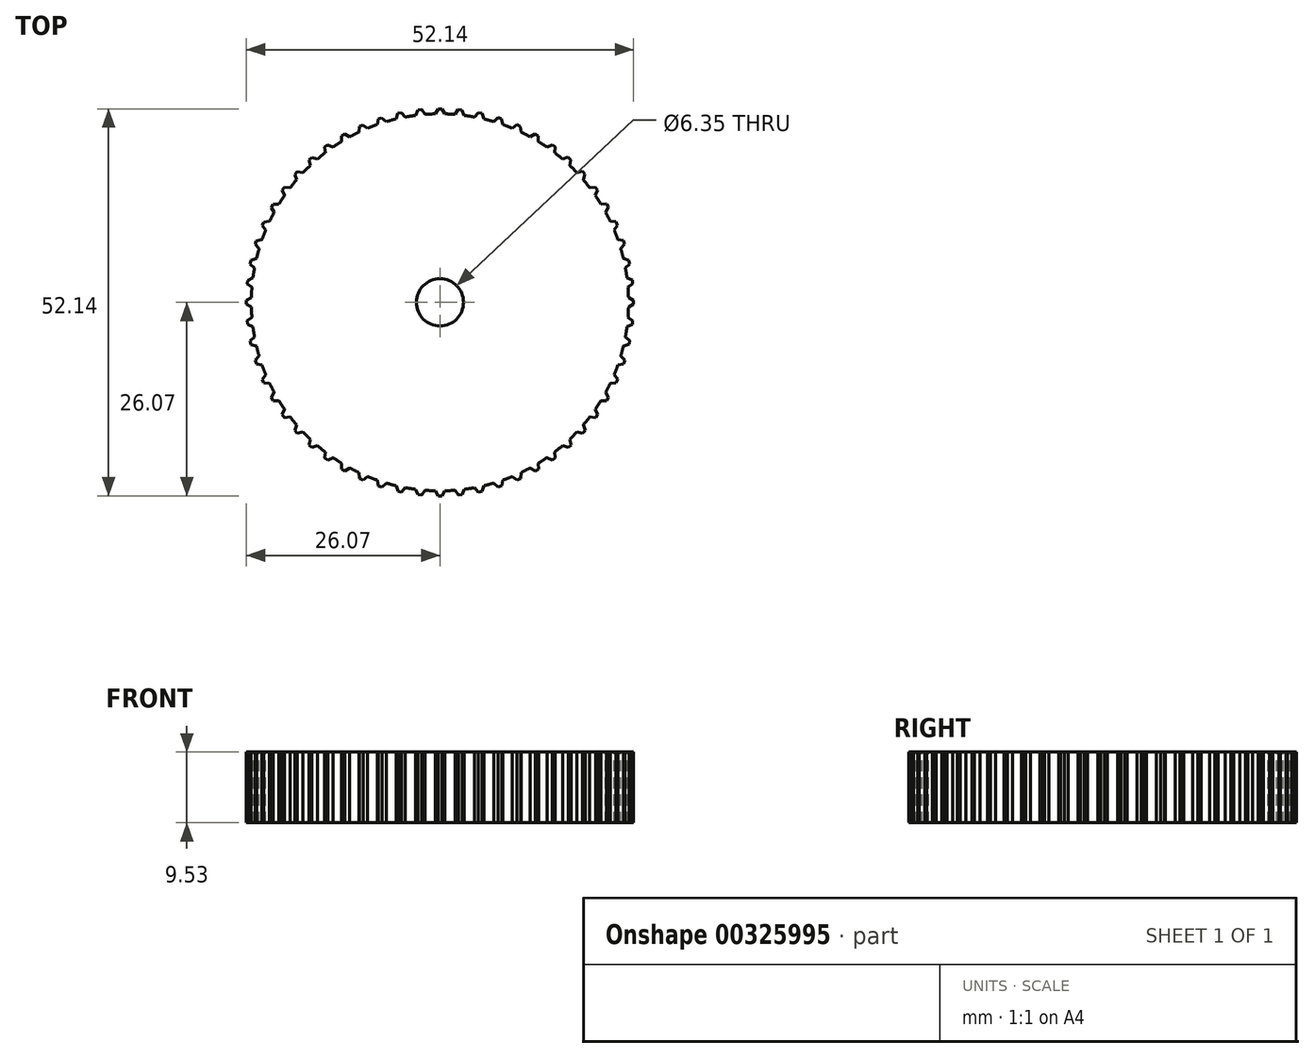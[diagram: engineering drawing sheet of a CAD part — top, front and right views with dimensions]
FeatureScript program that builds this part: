
annotation { "Feature Type Name" : "Feature", "Feature Type Description" : "" }
export const myFeature = defineFeature(function(context is Context, id is Id, definition is map)
    precondition{}
    {
        {
            var Q0;
            Q0=qCreatedBy(makeId("Top.planeOp"),FACE);
            var sketch = newSketch(context, id + "F0", { "sketchPlane" : qUnion([Q0])});
            skCircle(sketch, "E0", {"center": v(0, 0) * mm, "radius": 3.18 * mm});
            skCircle(sketch, "E1", {"center": v(0, 0) * mm, "radius": 25.4 * mm});
            skSolve(sketch);
        }
        {
            var Q0;
            Q0=makeQuery(id+"F0.imprint","IMPRINT",FACE,{"disambiguationData":[TD([[makeQuery(id+"F0.imprint","IMPRINT",EDGE,{"derivedFrom":sQuery(id+"F0.wireOp",EDGE,"E0")}),-1.0]])]});
            extrude(context, id + "F1", {"entities" : qUnion([Q0]), "depth" : 9.52 * mm});
        }
        {
            var Q0;
            Q0=makeQuery(id+"F1.opExtrude","CAP_FACE",FACE,{"disambiguationData":[OSD([sQuery(id+"F0.wireOp",EDGE,"E0"),sQuery(id+"F0.wireOp",EDGE,"E1")])],"isStart":false});
            var sketch = newSketch(context, id + "F2", { "sketchPlane" : qUnion([Q0])});
            skLineSegment(sketch, "E2", {"start": v(-0.64, 25.4) * mm, "end": v(-0.27, 26.07) * mm});
            skLineSegment(sketch, "E3", {"start": v(-0.27, 26.07) * mm, "end": v(0.24, 26.07) * mm});
            skLineSegment(sketch, "E4", {"start": v(0.24, 26.07) * mm, "end": v(0.63, 25.4) * mm});
            skLineSegment(sketch, "E5", {"start": v(0.64, 25.4) * mm, "end": v(-0.64, 25.4) * mm});
            skLineSegment(sketch, "E6.1.0", {"start": v(-2.02, 25.32) * mm, "end": v(-3.29, 25.19) * mm});
            skLineSegment(sketch, "E6.1.1", {"start": v(-2.99, 25.9) * mm, "end": v(-2.48, 25.95) * mm});
            skLineSegment(sketch, "E6.1.2", {"start": v(-2.48, 25.95) * mm, "end": v(-2.02, 25.32) * mm});
            skLineSegment(sketch, "E6.1.3", {"start": v(-3.29, 25.19) * mm, "end": v(-2.99, 25.9) * mm});
            skLineSegment(sketch, "E6.2.0", {"start": v(-4.66, 24.97) * mm, "end": v(-5.9, 24.7) * mm});
            skLineSegment(sketch, "E6.2.1", {"start": v(-5.68, 25.45) * mm, "end": v(-5.18, 25.55) * mm});
            skLineSegment(sketch, "E6.2.2", {"start": v(-5.18, 25.55) * mm, "end": v(-4.66, 24.97) * mm});
            skLineSegment(sketch, "E6.2.3", {"start": v(-5.9, 24.7) * mm, "end": v(-5.68, 25.45) * mm});
            skLineSegment(sketch, "E6.3.0", {"start": v(-7.24, 24.35) * mm, "end": v(-8.45, 23.95) * mm});
            skLineSegment(sketch, "E6.3.1", {"start": v(-8.3, 24.71) * mm, "end": v(-7.83, 24.87) * mm});
            skLineSegment(sketch, "E6.3.2", {"start": v(-7.83, 24.87) * mm, "end": v(-7.24, 24.35) * mm});
            skLineSegment(sketch, "E6.3.3", {"start": v(-8.45, 23.95) * mm, "end": v(-8.3, 24.71) * mm});
            skLineSegment(sketch, "E6.4.0", {"start": v(-9.75, 23.46) * mm, "end": v(-10.9, 22.94) * mm});
            skLineSegment(sketch, "E6.4.1", {"start": v(-10.85, 23.7) * mm, "end": v(-10.38, 23.92) * mm});
            skLineSegment(sketch, "E6.4.2", {"start": v(-10.38, 23.92) * mm, "end": v(-9.75, 23.46) * mm});
            skLineSegment(sketch, "E6.4.3", {"start": v(-10.9, 22.94) * mm, "end": v(-10.85, 23.7) * mm});
            skLineSegment(sketch, "E6.5.0", {"start": v(-12.15, 22.3) * mm, "end": v(-13.25, 21.67) * mm});
            skLineSegment(sketch, "E6.5.1", {"start": v(-13.27, 22.45) * mm, "end": v(-12.83, 22.7) * mm});
            skLineSegment(sketch, "E6.5.2", {"start": v(-12.83, 22.7) * mm, "end": v(-12.15, 22.3) * mm});
            skLineSegment(sketch, "E6.5.3", {"start": v(-13.25, 21.67) * mm, "end": v(-13.27, 22.45) * mm});
            skLineSegment(sketch, "E6.6.0", {"start": v(-14.41, 20.92) * mm, "end": v(-15.44, 20.17) * mm});
            skLineSegment(sketch, "E6.6.1", {"start": v(-15.54, 20.94) * mm, "end": v(-15.13, 21.23) * mm});
            skLineSegment(sketch, "E6.6.2", {"start": v(-15.13, 21.23) * mm, "end": v(-14.41, 20.92) * mm});
            skLineSegment(sketch, "E6.6.3", {"start": v(-15.44, 20.17) * mm, "end": v(-15.54, 20.94) * mm});
            skLineSegment(sketch, "E6.7.0", {"start": v(-16.52, 19.3) * mm, "end": v(-17.46, 18.45) * mm});
            skLineSegment(sketch, "E6.7.1", {"start": v(-17.64, 19.2) * mm, "end": v(-17.27, 19.54) * mm});
            skLineSegment(sketch, "E6.7.2", {"start": v(-17.27, 19.54) * mm, "end": v(-16.52, 19.3) * mm});
            skLineSegment(sketch, "E6.7.3", {"start": v(-17.46, 18.45) * mm, "end": v(-17.64, 19.2) * mm});
            skLineSegment(sketch, "E6.8.0", {"start": v(-18.45, 17.46) * mm, "end": v(-19.3, 16.52) * mm});
            skLineSegment(sketch, "E6.8.1", {"start": v(-19.55, 17.25) * mm, "end": v(-19.21, 17.63) * mm});
            skLineSegment(sketch, "E6.8.2", {"start": v(-19.21, 17.63) * mm, "end": v(-18.45, 17.46) * mm});
            skLineSegment(sketch, "E6.8.3", {"start": v(-19.3, 16.52) * mm, "end": v(-19.55, 17.25) * mm});
            skLineSegment(sketch, "E6.9.0", {"start": v(-20.17, 15.44) * mm, "end": v(-20.92, 14.41) * mm});
            skLineSegment(sketch, "E6.9.1", {"start": v(-21.25, 15.1) * mm, "end": v(-20.95, 15.52) * mm});
            skLineSegment(sketch, "E6.9.2", {"start": v(-20.95, 15.52) * mm, "end": v(-20.17, 15.44) * mm});
            skLineSegment(sketch, "E6.9.3", {"start": v(-20.92, 14.41) * mm, "end": v(-21.25, 15.1) * mm});
            skLineSegment(sketch, "E6.10.0", {"start": v(-21.67, 13.25) * mm, "end": v(-22.3, 12.15) * mm});
            skLineSegment(sketch, "E6.10.1", {"start": v(-22.71, 12.8) * mm, "end": v(-22.46, 13.25) * mm});
            skLineSegment(sketch, "E6.10.2", {"start": v(-22.46, 13.25) * mm, "end": v(-21.67, 13.25) * mm});
            skLineSegment(sketch, "E6.10.3", {"start": v(-22.3, 12.15) * mm, "end": v(-22.71, 12.8) * mm});
            skLineSegment(sketch, "E6.11.0", {"start": v(-22.94, 10.9) * mm, "end": v(-23.46, 9.75) * mm});
            skLineSegment(sketch, "E6.11.1", {"start": v(-23.93, 10.36) * mm, "end": v(-23.72, 10.83) * mm});
            skLineSegment(sketch, "E6.11.2", {"start": v(-23.72, 10.83) * mm, "end": v(-22.94, 10.9) * mm});
            skLineSegment(sketch, "E6.11.3", {"start": v(-23.46, 9.75) * mm, "end": v(-23.93, 10.36) * mm});
            skLineSegment(sketch, "E6.12.0", {"start": v(-23.95, 8.45) * mm, "end": v(-24.35, 7.24) * mm});
            skLineSegment(sketch, "E6.12.1", {"start": v(-24.88, 7.8) * mm, "end": v(-24.72, 8.29) * mm});
            skLineSegment(sketch, "E6.12.2", {"start": v(-24.72, 8.29) * mm, "end": v(-23.95, 8.45) * mm});
            skLineSegment(sketch, "E6.12.3", {"start": v(-24.35, 7.24) * mm, "end": v(-24.88, 7.8) * mm});
            skLineSegment(sketch, "E6.13.0", {"start": v(-24.7, 5.9) * mm, "end": v(-24.97, 4.66) * mm});
            skLineSegment(sketch, "E6.13.1", {"start": v(-25.56, 5.16) * mm, "end": v(-25.45, 5.66) * mm});
            skLineSegment(sketch, "E6.13.2", {"start": v(-25.45, 5.66) * mm, "end": v(-24.7, 5.9) * mm});
            skLineSegment(sketch, "E6.13.3", {"start": v(-24.97, 4.66) * mm, "end": v(-25.56, 5.16) * mm});
            skLineSegment(sketch, "E6.14.0", {"start": v(-25.19, 3.29) * mm, "end": v(-25.32, 2.02) * mm});
            skLineSegment(sketch, "E6.14.1", {"start": v(-25.96, 2.46) * mm, "end": v(-25.9, 2.97) * mm});
            skLineSegment(sketch, "E6.14.2", {"start": v(-25.9, 2.97) * mm, "end": v(-25.19, 3.29) * mm});
            skLineSegment(sketch, "E6.14.3", {"start": v(-25.32, 2.02) * mm, "end": v(-25.96, 2.46) * mm});
            skLineSegment(sketch, "E6.15.0", {"start": v(-25.4, 0.64) * mm, "end": v(-25.4, -0.63) * mm});
            skLineSegment(sketch, "E6.15.1", {"start": v(-26.07, -0.27) * mm, "end": v(-26.07, 0.24) * mm});
            skLineSegment(sketch, "E6.15.2", {"start": v(-26.07, 0.24) * mm, "end": v(-25.4, 0.64) * mm});
            skLineSegment(sketch, "E6.15.3", {"start": v(-25.4, -0.63) * mm, "end": v(-26.07, -0.27) * mm});
            skLineSegment(sketch, "E6.16.0", {"start": v(-25.32, -2.02) * mm, "end": v(-25.19, -3.29) * mm});
            skLineSegment(sketch, "E6.16.1", {"start": v(-25.9, -2.99) * mm, "end": v(-25.95, -2.48) * mm});
            skLineSegment(sketch, "E6.16.2", {"start": v(-25.95, -2.48) * mm, "end": v(-25.32, -2.02) * mm});
            skLineSegment(sketch, "E6.16.3", {"start": v(-25.19, -3.29) * mm, "end": v(-25.9, -2.99) * mm});
            skLineSegment(sketch, "E6.17.0", {"start": v(-24.97, -4.66) * mm, "end": v(-24.7, -5.9) * mm});
            skLineSegment(sketch, "E6.17.1", {"start": v(-25.45, -5.68) * mm, "end": v(-25.55, -5.18) * mm});
            skLineSegment(sketch, "E6.17.2", {"start": v(-25.55, -5.18) * mm, "end": v(-24.97, -4.66) * mm});
            skLineSegment(sketch, "E6.17.3", {"start": v(-24.7, -5.9) * mm, "end": v(-25.45, -5.68) * mm});
            skLineSegment(sketch, "E6.18.0", {"start": v(-24.35, -7.24) * mm, "end": v(-23.95, -8.45) * mm});
            skLineSegment(sketch, "E6.18.1", {"start": v(-24.71, -8.3) * mm, "end": v(-24.87, -7.83) * mm});
            skLineSegment(sketch, "E6.18.2", {"start": v(-24.87, -7.83) * mm, "end": v(-24.35, -7.24) * mm});
            skLineSegment(sketch, "E6.18.3", {"start": v(-23.95, -8.45) * mm, "end": v(-24.71, -8.3) * mm});
            skLineSegment(sketch, "E6.19.0", {"start": v(-23.46, -9.75) * mm, "end": v(-22.94, -10.9) * mm});
            skLineSegment(sketch, "E6.19.1", {"start": v(-23.7, -10.85) * mm, "end": v(-23.92, -10.38) * mm});
            skLineSegment(sketch, "E6.19.2", {"start": v(-23.92, -10.38) * mm, "end": v(-23.46, -9.75) * mm});
            skLineSegment(sketch, "E6.19.3", {"start": v(-22.94, -10.9) * mm, "end": v(-23.7, -10.85) * mm});
            skLineSegment(sketch, "E6.20.0", {"start": v(-22.3, -12.15) * mm, "end": v(-21.67, -13.25) * mm});
            skLineSegment(sketch, "E6.20.1", {"start": v(-22.45, -13.27) * mm, "end": v(-22.7, -12.83) * mm});
            skLineSegment(sketch, "E6.20.2", {"start": v(-22.7, -12.83) * mm, "end": v(-22.3, -12.15) * mm});
            skLineSegment(sketch, "E6.20.3", {"start": v(-21.67, -13.25) * mm, "end": v(-22.45, -13.27) * mm});
            skLineSegment(sketch, "E6.21.0", {"start": v(-20.92, -14.41) * mm, "end": v(-20.17, -15.44) * mm});
            skLineSegment(sketch, "E6.21.1", {"start": v(-20.94, -15.54) * mm, "end": v(-21.23, -15.13) * mm});
            skLineSegment(sketch, "E6.21.2", {"start": v(-21.23, -15.13) * mm, "end": v(-20.92, -14.41) * mm});
            skLineSegment(sketch, "E6.21.3", {"start": v(-20.17, -15.44) * mm, "end": v(-20.94, -15.54) * mm});
            skLineSegment(sketch, "E6.22.0", {"start": v(-19.3, -16.52) * mm, "end": v(-18.45, -17.46) * mm});
            skLineSegment(sketch, "E6.22.1", {"start": v(-19.2, -17.64) * mm, "end": v(-19.54, -17.27) * mm});
            skLineSegment(sketch, "E6.22.2", {"start": v(-19.54, -17.27) * mm, "end": v(-19.3, -16.52) * mm});
            skLineSegment(sketch, "E6.22.3", {"start": v(-18.45, -17.46) * mm, "end": v(-19.2, -17.64) * mm});
            skLineSegment(sketch, "E6.23.0", {"start": v(-17.46, -18.45) * mm, "end": v(-16.52, -19.3) * mm});
            skLineSegment(sketch, "E6.23.1", {"start": v(-17.25, -19.55) * mm, "end": v(-17.63, -19.21) * mm});
            skLineSegment(sketch, "E6.23.2", {"start": v(-17.63, -19.21) * mm, "end": v(-17.46, -18.45) * mm});
            skLineSegment(sketch, "E6.23.3", {"start": v(-16.52, -19.3) * mm, "end": v(-17.25, -19.55) * mm});
            skLineSegment(sketch, "E6.24.0", {"start": v(-15.44, -20.17) * mm, "end": v(-14.41, -20.92) * mm});
            skLineSegment(sketch, "E6.24.1", {"start": v(-15.1, -21.25) * mm, "end": v(-15.52, -20.95) * mm});
            skLineSegment(sketch, "E6.24.2", {"start": v(-15.52, -20.95) * mm, "end": v(-15.44, -20.17) * mm});
            skLineSegment(sketch, "E6.24.3", {"start": v(-14.41, -20.92) * mm, "end": v(-15.1, -21.25) * mm});
            skLineSegment(sketch, "E6.25.0", {"start": v(-13.25, -21.67) * mm, "end": v(-12.15, -22.3) * mm});
            skLineSegment(sketch, "E6.25.1", {"start": v(-12.8, -22.71) * mm, "end": v(-13.25, -22.46) * mm});
            skLineSegment(sketch, "E6.25.2", {"start": v(-13.25, -22.46) * mm, "end": v(-13.25, -21.67) * mm});
            skLineSegment(sketch, "E6.25.3", {"start": v(-12.15, -22.3) * mm, "end": v(-12.8, -22.71) * mm});
            skLineSegment(sketch, "E6.26.0", {"start": v(-10.9, -22.94) * mm, "end": v(-9.75, -23.46) * mm});
            skLineSegment(sketch, "E6.26.1", {"start": v(-10.36, -23.93) * mm, "end": v(-10.83, -23.72) * mm});
            skLineSegment(sketch, "E6.26.2", {"start": v(-10.83, -23.72) * mm, "end": v(-10.9, -22.94) * mm});
            skLineSegment(sketch, "E6.26.3", {"start": v(-9.75, -23.46) * mm, "end": v(-10.36, -23.93) * mm});
            skLineSegment(sketch, "E6.27.0", {"start": v(-8.45, -23.95) * mm, "end": v(-7.24, -24.35) * mm});
            skLineSegment(sketch, "E6.27.1", {"start": v(-7.8, -24.88) * mm, "end": v(-8.29, -24.72) * mm});
            skLineSegment(sketch, "E6.27.2", {"start": v(-8.29, -24.72) * mm, "end": v(-8.45, -23.95) * mm});
            skLineSegment(sketch, "E6.27.3", {"start": v(-7.24, -24.35) * mm, "end": v(-7.8, -24.88) * mm});
            skLineSegment(sketch, "E6.28.0", {"start": v(-5.9, -24.7) * mm, "end": v(-4.66, -24.97) * mm});
            skLineSegment(sketch, "E6.28.1", {"start": v(-5.16, -25.56) * mm, "end": v(-5.66, -25.45) * mm});
            skLineSegment(sketch, "E6.28.2", {"start": v(-5.66, -25.45) * mm, "end": v(-5.9, -24.7) * mm});
            skLineSegment(sketch, "E6.28.3", {"start": v(-4.66, -24.97) * mm, "end": v(-5.16, -25.56) * mm});
            skLineSegment(sketch, "E6.29.0", {"start": v(-3.29, -25.19) * mm, "end": v(-2.02, -25.32) * mm});
            skLineSegment(sketch, "E6.29.1", {"start": v(-2.46, -25.96) * mm, "end": v(-2.97, -25.9) * mm});
            skLineSegment(sketch, "E6.29.2", {"start": v(-2.97, -25.9) * mm, "end": v(-3.29, -25.19) * mm});
            skLineSegment(sketch, "E6.29.3", {"start": v(-2.02, -25.32) * mm, "end": v(-2.46, -25.96) * mm});
            skLineSegment(sketch, "E6.30.0", {"start": v(-0.64, -25.4) * mm, "end": v(0.63, -25.4) * mm});
            skLineSegment(sketch, "E6.30.1", {"start": v(0.27, -26.07) * mm, "end": v(-0.24, -26.07) * mm});
            skLineSegment(sketch, "E6.30.2", {"start": v(-0.24, -26.07) * mm, "end": v(-0.64, -25.4) * mm});
            skLineSegment(sketch, "E6.30.3", {"start": v(0.63, -25.4) * mm, "end": v(0.27, -26.07) * mm});
            skLineSegment(sketch, "E6.31.0", {"start": v(2.02, -25.32) * mm, "end": v(3.29, -25.19) * mm});
            skLineSegment(sketch, "E6.31.1", {"start": v(2.99, -25.9) * mm, "end": v(2.48, -25.95) * mm});
            skLineSegment(sketch, "E6.31.2", {"start": v(2.48, -25.95) * mm, "end": v(2.02, -25.32) * mm});
            skLineSegment(sketch, "E6.31.3", {"start": v(3.29, -25.19) * mm, "end": v(2.99, -25.9) * mm});
            skLineSegment(sketch, "E6.32.0", {"start": v(4.66, -24.97) * mm, "end": v(5.9, -24.7) * mm});
            skLineSegment(sketch, "E6.32.1", {"start": v(5.68, -25.45) * mm, "end": v(5.18, -25.55) * mm});
            skLineSegment(sketch, "E6.32.2", {"start": v(5.18, -25.55) * mm, "end": v(4.66, -24.97) * mm});
            skLineSegment(sketch, "E6.32.3", {"start": v(5.9, -24.7) * mm, "end": v(5.68, -25.45) * mm});
            skLineSegment(sketch, "E6.33.0", {"start": v(7.24, -24.35) * mm, "end": v(8.45, -23.95) * mm});
            skLineSegment(sketch, "E6.33.1", {"start": v(8.3, -24.71) * mm, "end": v(7.83, -24.87) * mm});
            skLineSegment(sketch, "E6.33.2", {"start": v(7.83, -24.87) * mm, "end": v(7.24, -24.35) * mm});
            skLineSegment(sketch, "E6.33.3", {"start": v(8.45, -23.95) * mm, "end": v(8.3, -24.71) * mm});
            skLineSegment(sketch, "E6.34.0", {"start": v(9.75, -23.46) * mm, "end": v(10.9, -22.94) * mm});
            skLineSegment(sketch, "E6.34.1", {"start": v(10.85, -23.7) * mm, "end": v(10.38, -23.92) * mm});
            skLineSegment(sketch, "E6.34.2", {"start": v(10.38, -23.92) * mm, "end": v(9.75, -23.46) * mm});
            skLineSegment(sketch, "E6.34.3", {"start": v(10.9, -22.94) * mm, "end": v(10.85, -23.7) * mm});
            skLineSegment(sketch, "E6.35.0", {"start": v(12.15, -22.3) * mm, "end": v(13.25, -21.67) * mm});
            skLineSegment(sketch, "E6.35.1", {"start": v(13.27, -22.45) * mm, "end": v(12.83, -22.7) * mm});
            skLineSegment(sketch, "E6.35.2", {"start": v(12.83, -22.7) * mm, "end": v(12.15, -22.3) * mm});
            skLineSegment(sketch, "E6.35.3", {"start": v(13.25, -21.67) * mm, "end": v(13.27, -22.45) * mm});
            skLineSegment(sketch, "E6.36.0", {"start": v(14.41, -20.92) * mm, "end": v(15.44, -20.17) * mm});
            skLineSegment(sketch, "E6.36.1", {"start": v(15.54, -20.94) * mm, "end": v(15.13, -21.23) * mm});
            skLineSegment(sketch, "E6.36.2", {"start": v(15.13, -21.23) * mm, "end": v(14.41, -20.92) * mm});
            skLineSegment(sketch, "E6.36.3", {"start": v(15.44, -20.17) * mm, "end": v(15.54, -20.94) * mm});
            skLineSegment(sketch, "E6.37.0", {"start": v(16.52, -19.3) * mm, "end": v(17.46, -18.45) * mm});
            skLineSegment(sketch, "E6.37.1", {"start": v(17.64, -19.2) * mm, "end": v(17.27, -19.54) * mm});
            skLineSegment(sketch, "E6.37.2", {"start": v(17.27, -19.54) * mm, "end": v(16.52, -19.3) * mm});
            skLineSegment(sketch, "E6.37.3", {"start": v(17.46, -18.45) * mm, "end": v(17.64, -19.2) * mm});
            skLineSegment(sketch, "E6.38.0", {"start": v(18.45, -17.46) * mm, "end": v(19.3, -16.52) * mm});
            skLineSegment(sketch, "E6.38.1", {"start": v(19.55, -17.25) * mm, "end": v(19.21, -17.63) * mm});
            skLineSegment(sketch, "E6.38.2", {"start": v(19.21, -17.63) * mm, "end": v(18.45, -17.46) * mm});
            skLineSegment(sketch, "E6.38.3", {"start": v(19.3, -16.52) * mm, "end": v(19.55, -17.25) * mm});
            skLineSegment(sketch, "E6.39.0", {"start": v(20.17, -15.44) * mm, "end": v(20.92, -14.41) * mm});
            skLineSegment(sketch, "E6.39.1", {"start": v(21.25, -15.1) * mm, "end": v(20.95, -15.52) * mm});
            skLineSegment(sketch, "E6.39.2", {"start": v(20.95, -15.52) * mm, "end": v(20.17, -15.44) * mm});
            skLineSegment(sketch, "E6.39.3", {"start": v(20.92, -14.41) * mm, "end": v(21.25, -15.1) * mm});
            skLineSegment(sketch, "E6.40.0", {"start": v(21.67, -13.25) * mm, "end": v(22.3, -12.15) * mm});
            skLineSegment(sketch, "E6.40.1", {"start": v(22.71, -12.8) * mm, "end": v(22.46, -13.25) * mm});
            skLineSegment(sketch, "E6.40.2", {"start": v(22.46, -13.25) * mm, "end": v(21.67, -13.25) * mm});
            skLineSegment(sketch, "E6.40.3", {"start": v(22.3, -12.15) * mm, "end": v(22.71, -12.8) * mm});
            skLineSegment(sketch, "E6.41.0", {"start": v(22.94, -10.9) * mm, "end": v(23.46, -9.75) * mm});
            skLineSegment(sketch, "E6.41.1", {"start": v(23.93, -10.36) * mm, "end": v(23.72, -10.83) * mm});
            skLineSegment(sketch, "E6.41.2", {"start": v(23.72, -10.83) * mm, "end": v(22.94, -10.9) * mm});
            skLineSegment(sketch, "E6.41.3", {"start": v(23.46, -9.75) * mm, "end": v(23.93, -10.36) * mm});
            skLineSegment(sketch, "E6.42.0", {"start": v(23.95, -8.45) * mm, "end": v(24.35, -7.24) * mm});
            skLineSegment(sketch, "E6.42.1", {"start": v(24.88, -7.8) * mm, "end": v(24.72, -8.29) * mm});
            skLineSegment(sketch, "E6.42.2", {"start": v(24.72, -8.29) * mm, "end": v(23.95, -8.45) * mm});
            skLineSegment(sketch, "E6.42.3", {"start": v(24.35, -7.24) * mm, "end": v(24.88, -7.8) * mm});
            skLineSegment(sketch, "E6.43.0", {"start": v(24.7, -5.9) * mm, "end": v(24.97, -4.66) * mm});
            skLineSegment(sketch, "E6.43.1", {"start": v(25.56, -5.16) * mm, "end": v(25.45, -5.66) * mm});
            skLineSegment(sketch, "E6.43.2", {"start": v(25.45, -5.66) * mm, "end": v(24.7, -5.9) * mm});
            skLineSegment(sketch, "E6.43.3", {"start": v(24.97, -4.66) * mm, "end": v(25.56, -5.16) * mm});
            skLineSegment(sketch, "E6.44.0", {"start": v(25.19, -3.29) * mm, "end": v(25.32, -2.02) * mm});
            skLineSegment(sketch, "E6.44.1", {"start": v(25.96, -2.46) * mm, "end": v(25.9, -2.97) * mm});
            skLineSegment(sketch, "E6.44.2", {"start": v(25.9, -2.97) * mm, "end": v(25.19, -3.29) * mm});
            skLineSegment(sketch, "E6.44.3", {"start": v(25.32, -2.02) * mm, "end": v(25.96, -2.46) * mm});
            skLineSegment(sketch, "E6.45.0", {"start": v(25.4, -0.64) * mm, "end": v(25.4, 0.63) * mm});
            skLineSegment(sketch, "E6.45.1", {"start": v(26.07, 0.27) * mm, "end": v(26.07, -0.24) * mm});
            skLineSegment(sketch, "E6.45.2", {"start": v(26.07, -0.24) * mm, "end": v(25.4, -0.64) * mm});
            skLineSegment(sketch, "E6.45.3", {"start": v(25.4, 0.63) * mm, "end": v(26.07, 0.27) * mm});
            skLineSegment(sketch, "E6.46.0", {"start": v(25.32, 2.02) * mm, "end": v(25.19, 3.29) * mm});
            skLineSegment(sketch, "E6.46.1", {"start": v(25.9, 2.99) * mm, "end": v(25.95, 2.48) * mm});
            skLineSegment(sketch, "E6.46.2", {"start": v(25.95, 2.48) * mm, "end": v(25.32, 2.02) * mm});
            skLineSegment(sketch, "E6.46.3", {"start": v(25.19, 3.29) * mm, "end": v(25.9, 2.99) * mm});
            skLineSegment(sketch, "E6.47.0", {"start": v(24.97, 4.66) * mm, "end": v(24.7, 5.9) * mm});
            skLineSegment(sketch, "E6.47.1", {"start": v(25.45, 5.68) * mm, "end": v(25.55, 5.18) * mm});
            skLineSegment(sketch, "E6.47.2", {"start": v(25.55, 5.18) * mm, "end": v(24.97, 4.66) * mm});
            skLineSegment(sketch, "E6.47.3", {"start": v(24.7, 5.9) * mm, "end": v(25.45, 5.68) * mm});
            skLineSegment(sketch, "E6.48.0", {"start": v(24.35, 7.24) * mm, "end": v(23.95, 8.45) * mm});
            skLineSegment(sketch, "E6.48.1", {"start": v(24.71, 8.3) * mm, "end": v(24.87, 7.83) * mm});
            skLineSegment(sketch, "E6.48.2", {"start": v(24.87, 7.83) * mm, "end": v(24.35, 7.24) * mm});
            skLineSegment(sketch, "E6.48.3", {"start": v(23.95, 8.45) * mm, "end": v(24.71, 8.3) * mm});
            skLineSegment(sketch, "E6.49.0", {"start": v(23.46, 9.75) * mm, "end": v(22.94, 10.9) * mm});
            skLineSegment(sketch, "E6.49.1", {"start": v(23.7, 10.85) * mm, "end": v(23.92, 10.38) * mm});
            skLineSegment(sketch, "E6.49.2", {"start": v(23.92, 10.38) * mm, "end": v(23.46, 9.75) * mm});
            skLineSegment(sketch, "E6.49.3", {"start": v(22.94, 10.9) * mm, "end": v(23.7, 10.85) * mm});
            skPoint(sketch, "E6.center", {"position": v(0, 0) * mm});
            skLineSegment(sketch, "E7.2.50.0", {"start": v(22.3, 12.15) * mm, "end": v(21.67, 13.25) * mm});
            skLineSegment(sketch, "E7.3.50.0", {"start": v(22.45, 13.27) * mm, "end": v(22.7, 12.83) * mm});
            skLineSegment(sketch, "E7.6.50.0", {"start": v(22.7, 12.83) * mm, "end": v(22.3, 12.15) * mm});
            skLineSegment(sketch, "E7.9.50.0", {"start": v(21.67, 13.25) * mm, "end": v(22.45, 13.27) * mm});
            skLineSegment(sketch, "E7.2.51.0", {"start": v(20.92, 14.41) * mm, "end": v(20.17, 15.44) * mm});
            skLineSegment(sketch, "E7.3.51.0", {"start": v(20.94, 15.54) * mm, "end": v(21.23, 15.13) * mm});
            skLineSegment(sketch, "E7.6.51.0", {"start": v(21.23, 15.13) * mm, "end": v(20.92, 14.41) * mm});
            skLineSegment(sketch, "E7.9.51.0", {"start": v(20.17, 15.44) * mm, "end": v(20.94, 15.54) * mm});
            skLineSegment(sketch, "E7.2.52.0", {"start": v(19.3, 16.52) * mm, "end": v(18.45, 17.46) * mm});
            skLineSegment(sketch, "E7.3.52.0", {"start": v(19.2, 17.64) * mm, "end": v(19.54, 17.27) * mm});
            skLineSegment(sketch, "E7.6.52.0", {"start": v(19.54, 17.27) * mm, "end": v(19.3, 16.52) * mm});
            skLineSegment(sketch, "E7.9.52.0", {"start": v(18.45, 17.46) * mm, "end": v(19.2, 17.64) * mm});
            skLineSegment(sketch, "E7.2.53.0", {"start": v(17.46, 18.45) * mm, "end": v(16.52, 19.3) * mm});
            skLineSegment(sketch, "E7.3.53.0", {"start": v(17.25, 19.55) * mm, "end": v(17.63, 19.21) * mm});
            skLineSegment(sketch, "E7.6.53.0", {"start": v(17.63, 19.21) * mm, "end": v(17.46, 18.45) * mm});
            skLineSegment(sketch, "E7.9.53.0", {"start": v(16.52, 19.3) * mm, "end": v(17.25, 19.55) * mm});
            skLineSegment(sketch, "E7.2.54.0", {"start": v(15.44, 20.17) * mm, "end": v(14.41, 20.92) * mm});
            skLineSegment(sketch, "E7.3.54.0", {"start": v(15.1, 21.25) * mm, "end": v(15.52, 20.95) * mm});
            skLineSegment(sketch, "E7.6.54.0", {"start": v(15.52, 20.95) * mm, "end": v(15.44, 20.17) * mm});
            skLineSegment(sketch, "E7.9.54.0", {"start": v(14.41, 20.92) * mm, "end": v(15.1, 21.25) * mm});
            skLineSegment(sketch, "E7.2.55.0", {"start": v(13.25, 21.67) * mm, "end": v(12.15, 22.3) * mm});
            skLineSegment(sketch, "E7.3.55.0", {"start": v(12.8, 22.71) * mm, "end": v(13.25, 22.46) * mm});
            skLineSegment(sketch, "E7.6.55.0", {"start": v(13.25, 22.46) * mm, "end": v(13.25, 21.67) * mm});
            skLineSegment(sketch, "E7.9.55.0", {"start": v(12.15, 22.3) * mm, "end": v(12.8, 22.71) * mm});
            skLineSegment(sketch, "E7.2.56.0", {"start": v(10.9, 22.94) * mm, "end": v(9.75, 23.46) * mm});
            skLineSegment(sketch, "E7.3.56.0", {"start": v(10.36, 23.93) * mm, "end": v(10.83, 23.72) * mm});
            skLineSegment(sketch, "E7.6.56.0", {"start": v(10.83, 23.72) * mm, "end": v(10.9, 22.94) * mm});
            skLineSegment(sketch, "E7.9.56.0", {"start": v(9.75, 23.46) * mm, "end": v(10.36, 23.93) * mm});
            skLineSegment(sketch, "E7.2.57.0", {"start": v(8.45, 23.95) * mm, "end": v(7.24, 24.35) * mm});
            skLineSegment(sketch, "E7.3.57.0", {"start": v(7.8, 24.88) * mm, "end": v(8.29, 24.72) * mm});
            skLineSegment(sketch, "E7.6.57.0", {"start": v(8.29, 24.72) * mm, "end": v(8.45, 23.95) * mm});
            skLineSegment(sketch, "E7.9.57.0", {"start": v(7.24, 24.35) * mm, "end": v(7.8, 24.88) * mm});
            skLineSegment(sketch, "E7.2.58.0", {"start": v(5.9, 24.7) * mm, "end": v(4.66, 24.97) * mm});
            skLineSegment(sketch, "E7.3.58.0", {"start": v(5.16, 25.56) * mm, "end": v(5.66, 25.45) * mm});
            skLineSegment(sketch, "E7.6.58.0", {"start": v(5.66, 25.45) * mm, "end": v(5.9, 24.7) * mm});
            skLineSegment(sketch, "E7.9.58.0", {"start": v(4.66, 24.97) * mm, "end": v(5.16, 25.56) * mm});
            skLineSegment(sketch, "E7.2.59.0", {"start": v(3.29, 25.19) * mm, "end": v(2.02, 25.32) * mm});
            skLineSegment(sketch, "E7.3.59.0", {"start": v(2.46, 25.96) * mm, "end": v(2.97, 25.9) * mm});
            skLineSegment(sketch, "E7.6.59.0", {"start": v(2.97, 25.9) * mm, "end": v(3.29, 25.19) * mm});
            skLineSegment(sketch, "E7.9.59.0", {"start": v(2.02, 25.32) * mm, "end": v(2.46, 25.96) * mm});
            skSolve(sketch);
        }
        {
            var Q0;
            Q0 = qSketchRegion(id + "F2", true);
            var Q1;
            Q1=makeQuery(id+"F1.opExtrude","CAP_FACE",FACE,{"disambiguationData":[OSD([sQuery(id+"F0.wireOp",EDGE,"E0"),sQuery(id+"F0.wireOp",EDGE,"E1")])],"isStart":true});
            extrude(context, id + "F3", {"entities" : qUnion([Q0]), "operationType" : NewBodyOperationType.ADD, "endBound" : BoundingType.UP_TO_SURFACE, "oppositeDirection" : true, "endBoundEntityFace" : qUnion([Q1]), "depth" : 25.4 * mm});
        }
    });
